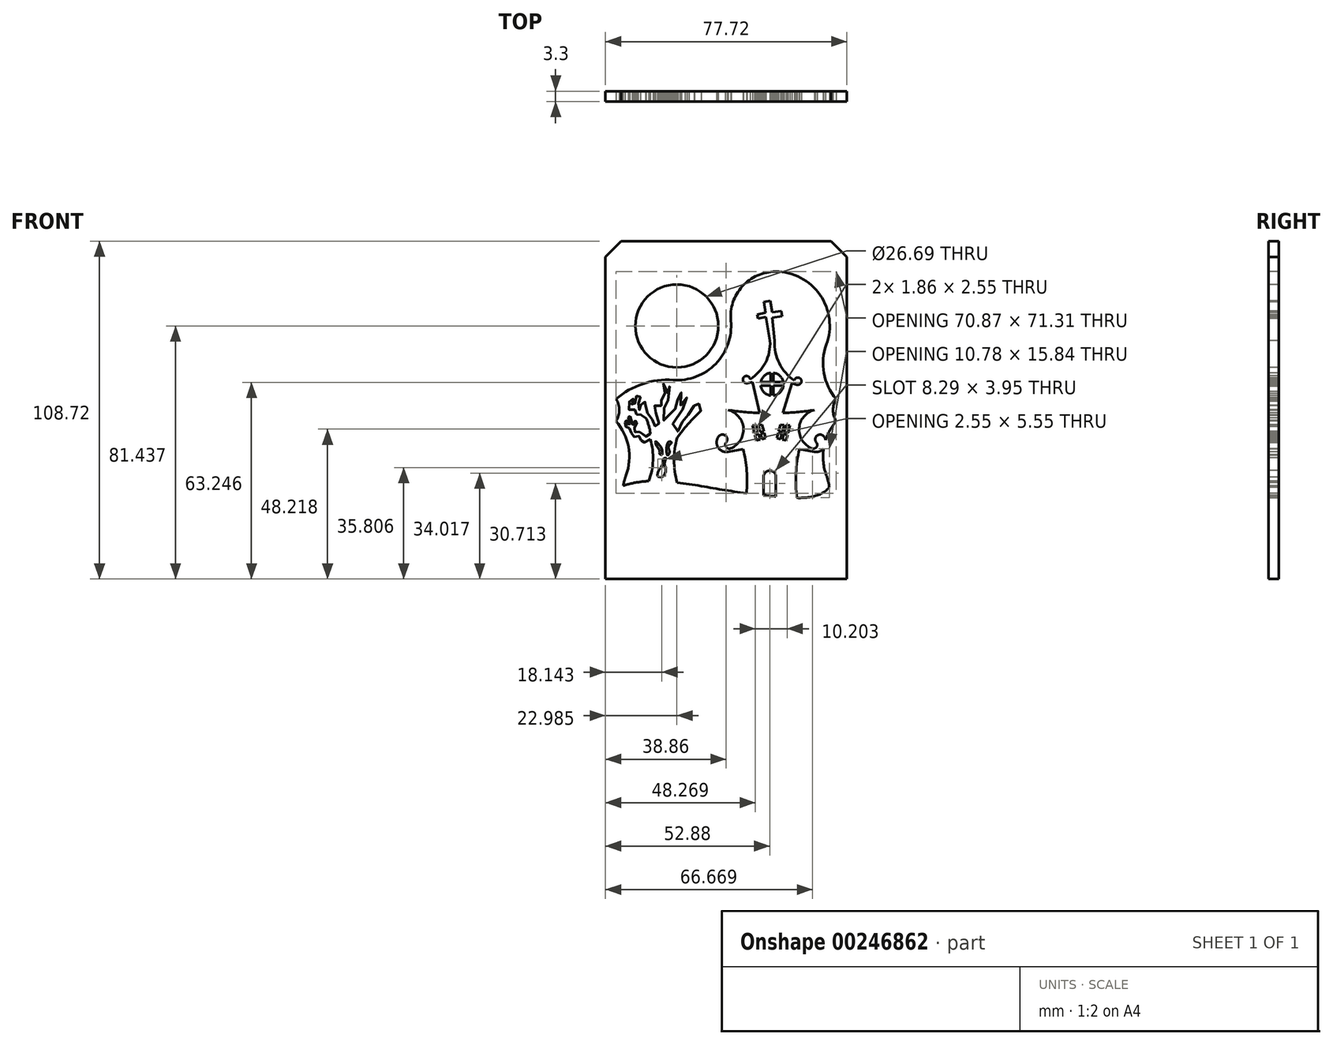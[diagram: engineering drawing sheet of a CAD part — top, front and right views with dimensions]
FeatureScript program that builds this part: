
annotation { "Feature Type Name" : "Feature", "Feature Type Description" : "" }
export const myFeature = defineFeature(function(context is Context, id is Id, definition is map)
    precondition{}
    {
        {
            var Q0;
            Q0=qCreatedBy(makeId("Front.planeOp"),FACE);
            var sketch = newSketch(context, id + "F0", { "sketchPlane" : qUnion([Q0])});
            skLineSegment(sketch, "E0.bottom", {"start": v(38.86, 54.36) * mm, "end": v(-38.86, 54.36) * mm});
            skLineSegment(sketch, "E0.top", {"start": v(38.86, -54.36) * mm, "end": v(-38.86, -54.36) * mm});
            skLineSegment(sketch, "E0.left", {"start": v(38.86, 54.36) * mm, "end": v(38.86, -54.36) * mm});
            skLineSegment(sketch, "E0.right", {"start": v(-38.86, 54.36) * mm, "end": v(-38.86, -54.36) * mm});
            skPoint(sketch, "E0.middle", {"position": v(0, 0) * mm});
            skSolve(sketch);
        }
        {
            var Q0;
            Q0 = qSketchRegion(id + "F0", true);
            extrude(context, id + "F1", {"entities" : qUnion([Q0]), "depth" : 3.3 * mm});
        }
        {
            var Q0;
            Q0=makeQuery(id+"F1.opExtrude","CAP_FACE",FACE,{"disambiguationData":[OSD([sQuery(id+"F0.wireOp",EDGE,"E0.bottom"),sQuery(id+"F0.wireOp",EDGE,"E0.top"),sQuery(id+"F0.wireOp",EDGE,"E0.left"),sQuery(id+"F0.wireOp",EDGE,"E0.right")])],"isStart":false});
            var sketch = newSketch(context, id + "F2", { "sketchPlane" : qUnion([Q0])});
            skLineSegment(sketch, "E1", {"start": v(0, 57.24) * mm, "end": v(0, -57.24) * mm, "construction": true});
            skLineSegment(sketch, "E2", {"start": v(-50.8, 0) * mm, "end": v(50.8, 0) * mm, "construction": true});
            skArc(sketch, "E3", {"start": v(35.44, -3.57) * mm, "mid": v(31.46, -11.87) * mm, "end": v(32.26, -21.03) * mm});
            skLineSegment(sketch, "E4", {"start": v(15.88, -44.54) * mm, "end": v(0, -44.54) * mm, "construction": true});
            skArc(sketch, "E5", {"start": v(15.88, -44.54) * mm, "mid": v(30.2, -37.06) * mm, "end": v(32.26, -21.03) * mm});
            skArc(sketch, "E6", {"start": v(15.88, -44.54) * mm, "mid": v(7.78, -45.34) * mm, "end": v(0, -47.71) * mm});
            skArc(sketch, "E7.MirrorCS", {"start": v(-15.87, -44.54) * mm, "mid": v(-7.78, -45.34) * mm, "end": v(0, -47.71) * mm});
            skArc(sketch, "E8.MirrorCS", {"start": v(-15.87, -44.54) * mm, "mid": v(-30.2, -37.06) * mm, "end": v(-32.26, -21.03) * mm});
            skArc(sketch, "E9.MirrorCS", {"start": v(-35.44, -3.57) * mm, "mid": v(-31.46, -11.87) * mm, "end": v(-32.26, -21.03) * mm});
            skArc(sketch, "E10.MirrorCS", {"start": v(-35.44, 3.57) * mm, "mid": v(-31.46, 11.87) * mm, "end": v(-32.26, 21.03) * mm});
            skArc(sketch, "E11.MirrorCS", {"start": v(-15.88, 44.54) * mm, "mid": v(-30.2, 37.06) * mm, "end": v(-32.26, 21.03) * mm});
            skArc(sketch, "E12.MirrorCS", {"start": v(-15.88, 44.54) * mm, "mid": v(-7.78, 45.34) * mm, "end": v(0, 47.71) * mm});
            skArc(sketch, "E13.MirrorCS", {"start": v(15.87, 44.54) * mm, "mid": v(7.78, 45.34) * mm, "end": v(0, 47.71) * mm});
            skArc(sketch, "E14.MirrorCS", {"start": v(15.87, 44.54) * mm, "mid": v(30.2, 37.06) * mm, "end": v(32.26, 21.03) * mm});
            skArc(sketch, "E15.MirrorCS", {"start": v(35.44, 3.57) * mm, "mid": v(31.46, 11.87) * mm, "end": v(32.26, 21.03) * mm});
            skArc(sketch, "E16", {"start": v(35.44, 3.57) * mm, "mid": v(34.41, 0) * mm, "end": v(35.44, -3.57) * mm});
            skPoint(sketch, "E17.orphan", {"position": v(39.69, 0) * mm});
            skArc(sketch, "E18.MirrorCS", {"start": v(-35.44, 3.57) * mm, "mid": v(-34.41, 0) * mm, "end": v(-35.44, -3.57) * mm});
            skPoint(sketch, "E19.orphan", {"position": v(-39.69, 0) * mm});
            skSolve(sketch);
        }
        {
            var Q0;
            {var subQ7=sQuery(id+"F2.wireOp",EDGE,"E5");Q0=makeQuery(id+"F2.imprint","IMPRINT",FACE,{"disambiguationData":[TD([[makeQuery(id+"F2.imprint","IMPRINT",EDGE,{"derivedFrom":subQ7}),1.0]])]});}
            extrude(context, id + "F3", {"entities" : qUnion([Q0]), "operationType" : NewBodyOperationType.REMOVE, "endBound" : BoundingType.THROUGH_ALL, "oppositeDirection" : true, "depth" : 25.4 * mm});
        }
        {
            var Q0;
            Q0=makeQuery(id+"F2.imprint","IMPRINT",FACE,{"disambiguationData":[TD([[makeQuery(id+"F2.imprint","IMPRINT",EDGE,{"derivedFrom":sQuery(id+"F2.wireOp",EDGE,"E3")}),1.0]])]});
            var sketch = newSketch(context, id + "F4", { "sketchPlane" : qUnion([Q0])});
            skFitSpline(sketch, "E20", {"points": [v(-34.74, -25) * mm, v(-17.68, -23.14) * mm, v(0, -25.84) * mm, v(18.3, -28) * mm, v(33.6, -24.4) * mm], "startDerivative": vector(68.08, 28.42) * mm, "endDerivative": vector(41.75, 55.86) * mm});
            skArc(sketch, "E21.0", {"start": v(15.88, -44.54) * mm, "mid": v(28.97, -38.63) * mm, "end": v(33.2, -24.9) * mm});
            skArc(sketch, "E22.0", {"start": v(-15.87, -44.54) * mm, "mid": v(-29.14, -38.43) * mm, "end": v(-33.13, -24.38) * mm});
            skArc(sketch, "E23.0", {"start": v(15.88, -44.54) * mm, "mid": v(7.78, -45.34) * mm, "end": v(0, -47.71) * mm});
            skArc(sketch, "E23.1", {"start": v(-15.87, -44.54) * mm, "mid": v(-7.78, -45.34) * mm, "end": v(0, -47.71) * mm});
            skPoint(sketch, "E24.orphan", {"position": v(-32.26, -21.03) * mm});
            skLineSegment(sketch, "E25.bottom", {"start": v(23.58, -32.65) * mm, "end": v(5.44, -32.65) * mm, "construction": true});
            skLineSegment(sketch, "E25.top", {"start": v(23.58, -12.55) * mm, "end": v(5.44, -12.55) * mm, "construction": true});
            skLineSegment(sketch, "E25.left", {"start": v(23.58, -32.65) * mm, "end": v(23.58, -12.55) * mm, "construction": true});
            skLineSegment(sketch, "E25.right", {"start": v(5.44, -32.65) * mm, "end": v(5.44, -12.55) * mm, "construction": true});
            skArc(sketch, "E26", {"start": v(6.5, -26.77) * mm, "mid": v(6.6, -19.6) * mm, "end": v(5.44, -12.55) * mm});
            skArc(sketch, "E27", {"start": v(23.58, -12.55) * mm, "mid": v(22.47, -20.37) * mm, "end": v(22.78, -28.26) * mm});
            skLineSegment(sketch, "E28", {"start": v(0.57, -13.45) * mm, "end": v(5.44, -12.55) * mm});
            skLineSegment(sketch, "E29", {"start": v(28.46, 0) * mm, "end": v(0.57, 0) * mm, "construction": true});
            skArc(sketch, "E30", {"start": v(-2.4, -8.48) * mm, "mid": v(-2.65, -12) * mm, "end": v(0.57, -13.45) * mm});
            skArc(sketch, "E31", {"start": v(0, -10.42) * mm, "mid": v(-0.23, -8.24) * mm, "end": v(-2.4, -8.48) * mm});
            skArc(sketch, "E32", {"start": v(0, -10.42) * mm, "mid": v(-0.04, -11.92) * mm, "end": v(1.4, -12.35) * mm});
            skArc(sketch, "E33", {"start": v(1.4, -12.35) * mm, "mid": v(5.55, -5.86) * mm, "end": v(0.57, 0) * mm});
            skLineSegment(sketch, "E34", {"start": v(14.51, 0) * mm, "end": v(14.51, -12.55) * mm, "construction": true});
            skArc(sketch, "E35.MirrorCS", {"start": v(27.61, -12.35) * mm, "mid": v(23.47, -5.86) * mm, "end": v(28.46, 0) * mm});
            skLineSegment(sketch, "E36.MirrorCS", {"start": v(28.46, -13.45) * mm, "end": v(23.58, -12.55) * mm});
            skArc(sketch, "E37.MirrorCS", {"start": v(31.42, -8.48) * mm, "mid": v(31.67, -12) * mm, "end": v(28.46, -13.45) * mm});
            skArc(sketch, "E38.MirrorCS", {"start": v(29.02, -10.42) * mm, "mid": v(29.25, -8.24) * mm, "end": v(31.42, -8.48) * mm});
            skArc(sketch, "E39.MirrorCS", {"start": v(29.02, -10.42) * mm, "mid": v(29.06, -11.92) * mm, "end": v(27.61, -12.35) * mm});
            skArc(sketch, "E40", {"start": v(0.57, 0) * mm, "mid": v(5.65, -0.6) * mm, "end": v(10.76, -0.93) * mm});
            skLineSegment(sketch, "E41", {"start": v(10.76, -0.93) * mm, "end": v(8.47, 9.06) * mm});
            skLineSegment(sketch, "E42", {"start": v(8.47, 9.06) * mm, "end": v(6.8, 8.68) * mm});
            skArc(sketch, "E43", {"start": v(7.7, 9.94) * mm, "mid": v(5.6, 10.49) * mm, "end": v(6.8, 8.68) * mm});
            skLineSegment(sketch, "E44", {"start": v(14.51, 0) * mm, "end": v(14.77, 8.31) * mm, "construction": true});
            skLineSegment(sketch, "E45.MirrorCS", {"start": v(18.26, -0.93) * mm, "end": v(21.1, 8.66) * mm});
            skLineSegment(sketch, "E46.MirrorCS", {"start": v(21.1, 8.66) * mm, "end": v(22.75, 8.18) * mm});
            skArc(sketch, "E47.MirrorCS", {"start": v(21.93, 9.5) * mm, "mid": v(24.07, 9.9) * mm, "end": v(22.75, 8.18) * mm});
            skArc(sketch, "E48", {"start": v(7.7, 9.94) * mm, "mid": v(12.62, 15.22) * mm, "end": v(14.1, 22.28) * mm});
            skArc(sketch, "E49", {"start": v(15.59, 22.28) * mm, "mid": v(17.1, 15.06) * mm, "end": v(21.93, 9.5) * mm});
            skLineSegment(sketch, "E50", {"start": v(14.1, 22.28) * mm, "end": v(12.75, 29.94) * mm});
            skLineSegment(sketch, "E51", {"start": v(12.75, 29.94) * mm, "end": v(10.25, 29.5) * mm});
            skLineSegment(sketch, "E52", {"start": v(10.25, 29.5) * mm, "end": v(10.04, 30.72) * mm});
            skLineSegment(sketch, "E53", {"start": v(10.04, 30.72) * mm, "end": v(12.66, 31.3) * mm});
            skLineSegment(sketch, "E54", {"start": v(12.66, 31.3) * mm, "end": v(12.12, 34.79) * mm});
            skLineSegment(sketch, "E55", {"start": v(12.12, 34.79) * mm, "end": v(14.24, 35.11) * mm});
            skLineSegment(sketch, "E56", {"start": v(14.24, 35.11) * mm, "end": v(14.8, 31.45) * mm});
            skLineSegment(sketch, "E57", {"start": v(14.8, 31.45) * mm, "end": v(17.72, 31.9) * mm});
            skLineSegment(sketch, "E58", {"start": v(17.72, 31.9) * mm, "end": v(17.99, 30.17) * mm});
            skLineSegment(sketch, "E59", {"start": v(17.99, 30.17) * mm, "end": v(14.89, 29.68) * mm});
            skLineSegment(sketch, "E60", {"start": v(14.89, 29.68) * mm, "end": v(15.59, 22.28) * mm});
            skArc(sketch, "E61.trimOffspring", {"start": v(18.26, -0.93) * mm, "mid": v(23.37, -0.6) * mm, "end": v(28.46, 0) * mm});
            skPoint(sketch, "E62.orphan", {"position": v(18.2, -1.17) * mm});
            skLineSegment(sketch, "E63", {"start": v(8.48, -4.98) * mm, "end": v(9.12, -7.41) * mm});
            skLineSegment(sketch, "E64", {"start": v(9.77, -9.85) * mm, "end": v(10.94, -9.54) * mm});
            skLineSegment(sketch, "E65", {"start": v(12.72, -9.06) * mm, "end": v(12.26, -7.34) * mm});
            skLineSegment(sketch, "E66", {"start": v(11.56, -4.7) * mm, "end": v(10.33, -4.82) * mm});
            skLineSegment(sketch, "E67", {"start": v(9.75, -4.87) * mm, "end": v(10.34, -7.13) * mm});
            skLineSegment(sketch, "E68", {"start": v(10.34, -7.13) * mm, "end": v(9.12, -7.41) * mm});
            skLineSegment(sketch, "E69", {"start": v(10.33, -4.82) * mm, "end": v(10.9, -7.06) * mm});
            skLineSegment(sketch, "E70", {"start": v(10.9, -7.06) * mm, "end": v(12.14, -6.89) * mm});
            skLineSegment(sketch, "E71", {"start": v(9.29, -8.05) * mm, "end": v(10.46, -7.73) * mm});
            skLineSegment(sketch, "E72", {"start": v(10.46, -7.73) * mm, "end": v(10.94, -9.54) * mm});
            skLineSegment(sketch, "E73", {"start": v(11.57, -9.37) * mm, "end": v(11.12, -7.64) * mm});
            skLineSegment(sketch, "E74", {"start": v(11.12, -7.64) * mm, "end": v(12.26, -7.34) * mm});
            skLineSegment(sketch, "E75.trimOffspring", {"start": v(12.14, -6.89) * mm, "end": v(11.56, -4.7) * mm});
            skLineSegment(sketch, "E76.trimOffspring", {"start": v(9.75, -4.87) * mm, "end": v(8.48, -4.98) * mm});
            skLineSegment(sketch, "E77.trimOffspring", {"start": v(9.29, -8.05) * mm, "end": v(9.77, -9.85) * mm});
            skLineSegment(sketch, "E78.trimOffspring", {"start": v(11.57, -9.37) * mm, "end": v(12.72, -9.06) * mm});
            skLineSegment(sketch, "E79.MirrorCS", {"start": v(17.46, -4.7) * mm, "end": v(18.69, -4.82) * mm});
            skLineSegment(sketch, "E80.MirrorCS", {"start": v(19.27, -4.87) * mm, "end": v(18.68, -7.13) * mm});
            skLineSegment(sketch, "E81.MirrorCS", {"start": v(17.45, -9.37) * mm, "end": v(17.9, -7.64) * mm});
            skLineSegment(sketch, "E82.MirrorCS", {"start": v(18.68, -7.13) * mm, "end": v(19.9, -7.41) * mm});
            skLineSegment(sketch, "E83.MirrorCS", {"start": v(17.9, -7.64) * mm, "end": v(16.76, -7.34) * mm});
            skLineSegment(sketch, "E84.MirrorCS", {"start": v(18.69, -4.82) * mm, "end": v(18.12, -7.06) * mm});
            skLineSegment(sketch, "E85.MirrorCS", {"start": v(16.88, -6.89) * mm, "end": v(17.46, -4.7) * mm});
            skLineSegment(sketch, "E86.MirrorCS", {"start": v(18.12, -7.06) * mm, "end": v(16.88, -6.89) * mm});
            skLineSegment(sketch, "E87.MirrorCS", {"start": v(19.27, -4.87) * mm, "end": v(20.54, -4.98) * mm});
            skLineSegment(sketch, "E88.MirrorCS", {"start": v(20.54, -4.98) * mm, "end": v(19.9, -7.41) * mm});
            skLineSegment(sketch, "E89.MirrorCS", {"start": v(19.73, -8.05) * mm, "end": v(18.56, -7.73) * mm});
            skLineSegment(sketch, "E90.MirrorCS", {"start": v(19.73, -8.05) * mm, "end": v(19.25, -9.85) * mm});
            skLineSegment(sketch, "E91.MirrorCS", {"start": v(19.25, -9.85) * mm, "end": v(18.08, -9.54) * mm});
            skLineSegment(sketch, "E92.MirrorCS", {"start": v(18.56, -7.73) * mm, "end": v(18.08, -9.54) * mm});
            skLineSegment(sketch, "E93.MirrorCS", {"start": v(17.45, -9.37) * mm, "end": v(16.3, -9.06) * mm});
            skLineSegment(sketch, "E94.MirrorCS", {"start": v(16.3, -9.06) * mm, "end": v(16.76, -7.34) * mm});
            skArc(sketch, "E95", {"start": v(14.28, 11.97) * mm, "mid": v(12.23, 10.98) * mm, "end": v(11.15, 8.98) * mm});
            skLineSegment(sketch, "E96", {"start": v(14.28, 11.97) * mm, "end": v(14.28, 8.98) * mm});
            skLineSegment(sketch, "E97", {"start": v(15.17, 4.65) * mm, "end": v(15.17, 7.88) * mm});
            skLineSegment(sketch, "E98", {"start": v(18.4, 8.98) * mm, "end": v(15.17, 8.98) * mm});
            skLineSegment(sketch, "E99", {"start": v(11.1, 7.88) * mm, "end": v(14.28, 7.88) * mm});
            skLineSegment(sketch, "E100.trimOffspring", {"start": v(15.17, 8.98) * mm, "end": v(15.17, 11.98) * mm});
            skLineSegment(sketch, "E101.trimOffspring", {"start": v(15.17, 7.88) * mm, "end": v(18.43, 7.88) * mm});
            skLineSegment(sketch, "E102.trimOffspring", {"start": v(14.28, 7.88) * mm, "end": v(14.28, 4.66) * mm});
            skLineSegment(sketch, "E103.trimOffspring", {"start": v(14.28, 8.98) * mm, "end": v(11.15, 8.98) * mm});
            skArc(sketch, "E104.trimOffspring", {"start": v(11.1, 7.88) * mm, "mid": v(12.14, 5.73) * mm, "end": v(14.28, 4.66) * mm});
            skArc(sketch, "E105.trimOffspring", {"start": v(18.4, 8.98) * mm, "mid": v(17.28, 11.01) * mm, "end": v(15.17, 11.98) * mm});
            skArc(sketch, "E106.trimOffspring", {"start": v(15.17, 4.65) * mm, "mid": v(17.37, 5.7) * mm, "end": v(18.43, 7.88) * mm});
            skLineSegment(sketch, "E107.left", {"start": v(12.04, -27.4) * mm, "end": v(12.04, -21.48) * mm});
            skLineSegment(sketch, "E107.right", {"start": v(16, -27.8) * mm, "end": v(16, -21.48) * mm});
            skArc(sketch, "E108", {"start": v(16, -21.48) * mm, "mid": v(14.02, -19.5) * mm, "end": v(12.04, -21.48) * mm});
            skLineSegment(sketch, "E109", {"start": v(12.04, -27.4) * mm, "end": v(16, -27.8) * mm});
            skArc(sketch, "E110.0", {"start": v(-35.44, -3.57) * mm, "mid": v(-31.46, -11.87) * mm, "end": v(-32.26, -21.03) * mm, "construction": true});
            skArc(sketch, "E110.1", {"start": v(15.87, 44.54) * mm, "mid": v(7.78, 45.34) * mm, "end": v(0, 47.71) * mm});
            skArc(sketch, "E110.2", {"start": v(-15.88, 44.54) * mm, "mid": v(-30.2, 37.06) * mm, "end": v(-32.26, 21.03) * mm, "construction": true});
            skArc(sketch, "E110.3", {"start": v(-35.44, 3.57) * mm, "mid": v(-34.41, 0) * mm, "end": v(-35.44, -3.57) * mm, "construction": true});
            skArc(sketch, "E110.4", {"start": v(-35.44, 3.57) * mm, "mid": v(-31.46, 11.87) * mm, "end": v(-32.26, 21.03) * mm});
            skArc(sketch, "E110.5", {"start": v(-15.88, 44.54) * mm, "mid": v(-7.78, 45.34) * mm, "end": v(0, 47.71) * mm});
            skArc(sketch, "E111", {"start": v(-17.1, 9.66) * mm, "mid": v(-3.37, 14.89) * mm, "end": v(1.5, 28.74) * mm});
            skArc(sketch, "E112", {"start": v(-17.1, 9.66) * mm, "mid": v(-26.87, 8.42) * mm, "end": v(-35.44, 3.57) * mm});
            skArc(sketch, "E113", {"start": v(15.87, 44.54) * mm, "mid": v(5.2, 39.82) * mm, "end": v(1.5, 28.74) * mm});
            skArc(sketch, "E114.trimOffspring", {"start": v(-15.88, 44.54) * mm, "mid": v(-30.2, 37.06) * mm, "end": v(-32.26, 21.03) * mm});
            skArc(sketch, "E115", {"start": v(-24.92, -22.89) * mm, "mid": v(-23.55, -16.2) * mm, "end": v(-24.4, -9.44) * mm});
            skFitSpline(sketch, "E116", {"points": [v(-24.4, -9.44) * mm, v(-26.98, -10.38) * mm, v(-27.97, -8.39) * mm, v(-29.93, -8.52) * mm, v(-30.92, -6) * mm, v(-32.1, -5.52) * mm, v(-32.53, -4.18) * mm, v(-32.18, -3.27) * mm, v(-31.84, -4.44) * mm, v(-31.05, -4.83) * mm, v(-31.49, -2) * mm, v(-30.88, -2.14) * mm, v(-30.1, -5.05) * mm, v(-29.45, -3.57) * mm, v(-28.71, -3.66) * mm, v(-29.54, -5.78) * mm, v(-29.23, -7.17) * mm, v(-27.54, -7.04) * mm, v(-26.28, -8.52) * mm, v(-24.4, -7.6) * mm], "startDerivative": vector(-46.53, -30.94) * mm, "endDerivative": vector(36.03, 29.74) * mm});
            skArc(sketch, "E117", {"start": v(-24.4, -7.6) * mm, "mid": v(-24.93, -4.98) * mm, "end": v(-25.9, -2.49) * mm});
            skFitSpline(sketch, "E118", {"points": [v(-25.9, -2.49) * mm, v(-27.5, -1.49) * mm, v(-28.76, -1.49) * mm, v(-29.23, 0) * mm, v(-31.14, 0) * mm, v(-30.8, 3.42) * mm, v(-29.97, 3.55) * mm, v(-30.27, 1.77) * mm, v(-29.54, 1.72) * mm, v(-28.8, 4.59) * mm, v(-27.67, 4.37) * mm, v(-28.28, 1.98) * mm, v(-27.84, 0) * mm, v(-27.2, 2.46) * mm, v(-25.9, 2.37) * mm, v(-25.9, 0) * mm, v(-24.11, -2.49) * mm, v(-22.72, -5.26) * mm, v(-21.68, -4.18) * mm, v(-23.16, 1.33) * mm, v(-20.82, 1.46) * mm, v(-20.82, 3.02) * mm], "startDerivative": vector(-33.14, 31.82) * mm, "endDerivative": vector(-15.18, 49.9) * mm});
            skFitSpline(sketch, "E119", {"points": [v(-20.82, 3.02) * mm, v(-19.2, 3.92) * mm, v(-20.04, 5.84) * mm, v(-20.82, 8.3) * mm, v(-20.04, 8.38) * mm, v(-19.62, 6.46) * mm, v(-18.62, 5.34) * mm, v(-18.96, 7.3) * mm, v(-18.2, 7.55) * mm, v(-18.12, 4.13) * mm, v(-19.33, 2.25) * mm, v(-19.46, 0.87) * mm, v(-20.82, 0) * mm, v(-20.04, -3.35) * mm, v(-16.32, 0) * mm, v(-17.1, 1.46) * mm, v(-15.74, 3.02) * mm, v(-15.45, 5.84) * mm, v(-14.49, 5.55) * mm, v(-14.82, 3.02) * mm, v(-14.53, 1.46) * mm, v(-13.36, 4) * mm, v(-12.02, 3.02) * mm, v(-14.2, 0) * mm, v(-17.1, -4.06) * mm, v(-17.1, -7.4) * mm, v(-14.36, -5.44) * mm, v(-14.57, -4.1) * mm, v(-12.78, -3.22) * mm, v(-12.53, -1.68) * mm, v(-10.44, -0.8) * mm, v(-10.27, 1.46) * mm, v(-9.35, 0) * mm, v(-8.6, 3.02) * mm, v(-8.1, 0) * mm, v(-9.44, -1.26) * mm, v(-11.31, -3.26) * mm, v(-13.15, -4.6) * mm, v(-13.36, -6.6) * mm, v(-15.78, -8.94) * mm], "startDerivative": vector(94.65, 30.69) * mm, "endDerivative": vector(-102.82, -69.25) * mm});
            skArc(sketch, "E120", {"start": v(-15.78, -8.94) * mm, "mid": v(-16.8, -16.14) * mm, "end": v(-15.78, -23.34) * mm});
            skFitSpline(sketch, "E121", {"points": [v(-22.4, -11.55) * mm, v(-21.43, -13.07) * mm, v(-21.4, -14.11) * mm, v(-20.72, -14.36) * mm, v(-20.54, -13.59) * mm, v(-20.94, -12.02) * mm, v(-21.71, -11.06) * mm, v(-22.67, -10.07) * mm, v(-22.4, -11.55) * mm]});
            skFitSpline(sketch, "E122", {"points": [v(-18.38, -10.1) * mm, v(-19.09, -11.5) * mm, v(-19.21, -12.7) * mm, v(-19.15, -14.02) * mm, v(-18.84, -14.6) * mm, v(-18.38, -14.05) * mm, v(-18.26, -13.1) * mm, v(-18.56, -12.32) * mm, v(-18.29, -11.28) * mm, v(-17.6, -10.38) * mm, v(-18.38, -10.1) * mm]});
            skFitSpline(sketch, "E123", {"points": [v(-20.3, -15.78) * mm, v(-20.35, -17.1) * mm, v(-20.9, -18.47) * mm, v(-21.8, -19.67) * mm, v(-21.9, -21.46) * mm, v(-20.45, -21.43) * mm, v(-19.64, -20.38) * mm, v(-19.43, -18.84) * mm, v(-19.7, -17.85) * mm, v(-19.7, -16.37) * mm, v(-19.43, -15.38) * mm, v(-20.3, -15.78) * mm]});
            skCircle(sketch, "E124", {"center": v(-15.88, 27.08) * mm, "radius": 13.34 * mm});
            skSolve(sketch);
        }
        {
            var Q0;
            Q0 = qSketchRegion(id + "F4", true);
            extrude(context, id + "F5", {"entities" : qUnion([Q0]), "operationType" : NewBodyOperationType.ADD, "oppositeDirection" : true, "depth" : 3.3 * mm});
        }
        {
            var Q0;
            Q0=makeQuery(id+"F1.opExtrude","SWEPT_EDGE",EDGE,{"disambiguationData":[OSD([sQuery(id+"F0.wireOp",EDGE,"E0.bottom"),sQuery(id+"F0.wireOp",EDGE,"E0.right")])]});
            var Q1;
            Q1=makeQuery(id+"F1.opExtrude","SWEPT_EDGE",EDGE,{"disambiguationData":[OSD([sQuery(id+"F0.wireOp",EDGE,"E0.bottom"),sQuery(id+"F0.wireOp",EDGE,"E0.left")])]});
            chamfer(context, id + "F6", {"entities" : qUnion([Q0, Q1]), "width" : 5.08 * mm, "tangentPropagation" : true});
        }
    });
